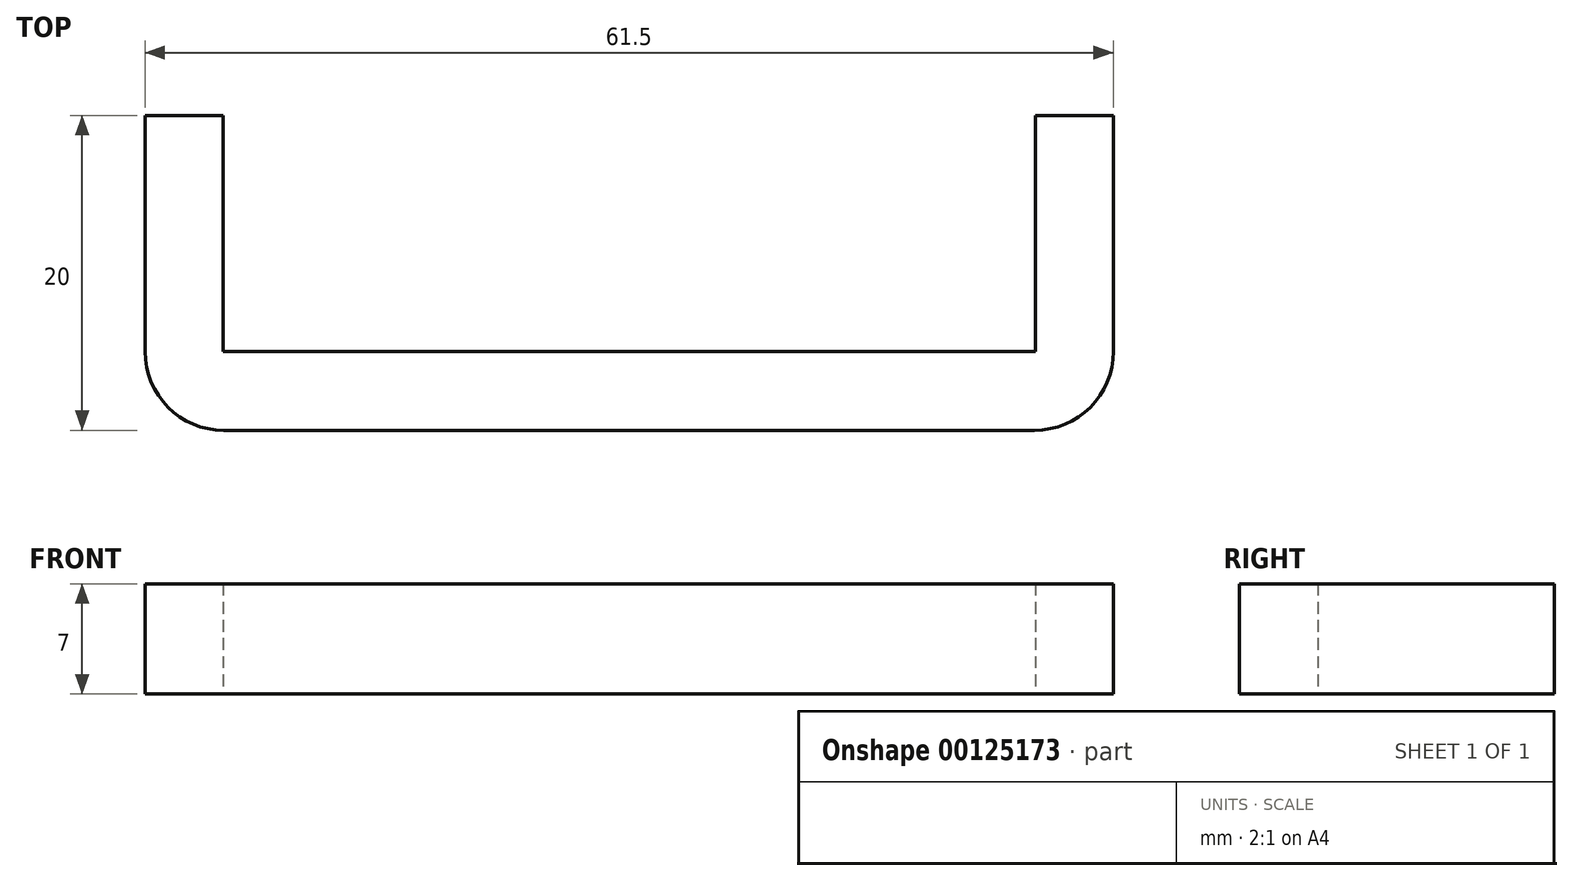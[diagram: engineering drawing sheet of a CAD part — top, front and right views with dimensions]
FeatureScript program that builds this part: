
annotation { "Feature Type Name" : "Feature", "Feature Type Description" : "" }
export const myFeature = defineFeature(function(context is Context, id is Id, definition is map)
    precondition{}
    {
        {
            var Q0;
            Q0=qCreatedBy(makeId("Top.planeOp"),FACE);
            var sketch = newSketch(context, id + "F0", { "sketchPlane" : qUnion([Q0])});
            skLineSegment(sketch, "E0.bottom", {"start": v(30.75, 10) * mm, "end": v(-30.75, 10) * mm});
            skLineSegment(sketch, "E0.top", {"start": v(25.75, -10) * mm, "end": v(-25.75, -10) * mm});
            skLineSegment(sketch, "E0.left", {"start": v(30.75, 10) * mm, "end": v(30.75, -5) * mm});
            skLineSegment(sketch, "E0.right", {"start": v(-30.75, 10) * mm, "end": v(-30.75, -5) * mm});
            skPoint(sketch, "E0.middle", {"position": v(0, 0) * mm});
            skLineSegment(sketch, "E1.bottom", {"start": v(25.8, 10) * mm, "end": v(-25.8, 10) * mm});
            skLineSegment(sketch, "E1.top", {"start": v(25.8, -5) * mm, "end": v(-25.8, -5) * mm});
            skLineSegment(sketch, "E1.left", {"start": v(25.8, 10) * mm, "end": v(25.8, -5) * mm});
            skLineSegment(sketch, "E1.right", {"start": v(-25.8, 10) * mm, "end": v(-25.8, -5) * mm});
            skPoint(sketch, "E1.middle", {"position": v(0, 2.5) * mm});
            skPoint(sketch, "E2.visualSharp", {"position": v(-30.75, -10) * mm});
            skArc(sketch, "E2.filletArc", {"start": v(-30.75, -5) * mm, "mid": v(-29.29, -8.54) * mm, "end": v(-25.75, -10) * mm});
            skPoint(sketch, "E3.visualSharp", {"position": v(30.75, -10) * mm});
            skArc(sketch, "E3.filletArc", {"start": v(25.75, -10) * mm, "mid": v(29.29, -8.54) * mm, "end": v(30.75, -5) * mm});
            skSolve(sketch);
        }
        {
            var Q0;
            Q0=makeQuery(id+"F0.imprint","IMPRINT",FACE,{"disambiguationData":[TD([[makeQuery(id+"F0.imprint","IMPRINT",EDGE,{"derivedFrom":sQuery(id+"F0.wireOp",EDGE,"E0.top")}),-1.0]])]});
            extrude(context, id + "F1", {"entities" : qUnion([Q0]), "depth" : 6 * mm});
        }
        {
            var Q0;
            Q0=makeQuery(id+"F0.imprint","IMPRINT",FACE,{"disambiguationData":[TD([[makeQuery(id+"F0.imprint","IMPRINT",EDGE,{"derivedFrom":sQuery(id+"F0.wireOp",EDGE,"E1.bottom")}),1.0]])]});
            var Q1;
            Q1=makeQuery(id+"F0.imprint","IMPRINT",FACE,{"disambiguationData":[TD([[makeQuery(id+"F0.imprint","IMPRINT",EDGE,{"derivedFrom":sQuery(id+"F0.wireOp",EDGE,"E0.top")}),-1.0]])]});
            extrude(context, id + "F2", {"entities" : qUnion([Q0, Q1]), "operationType" : NewBodyOperationType.ADD, "oppositeDirection" : true, "depth" : 1 * mm});
        }
    });
